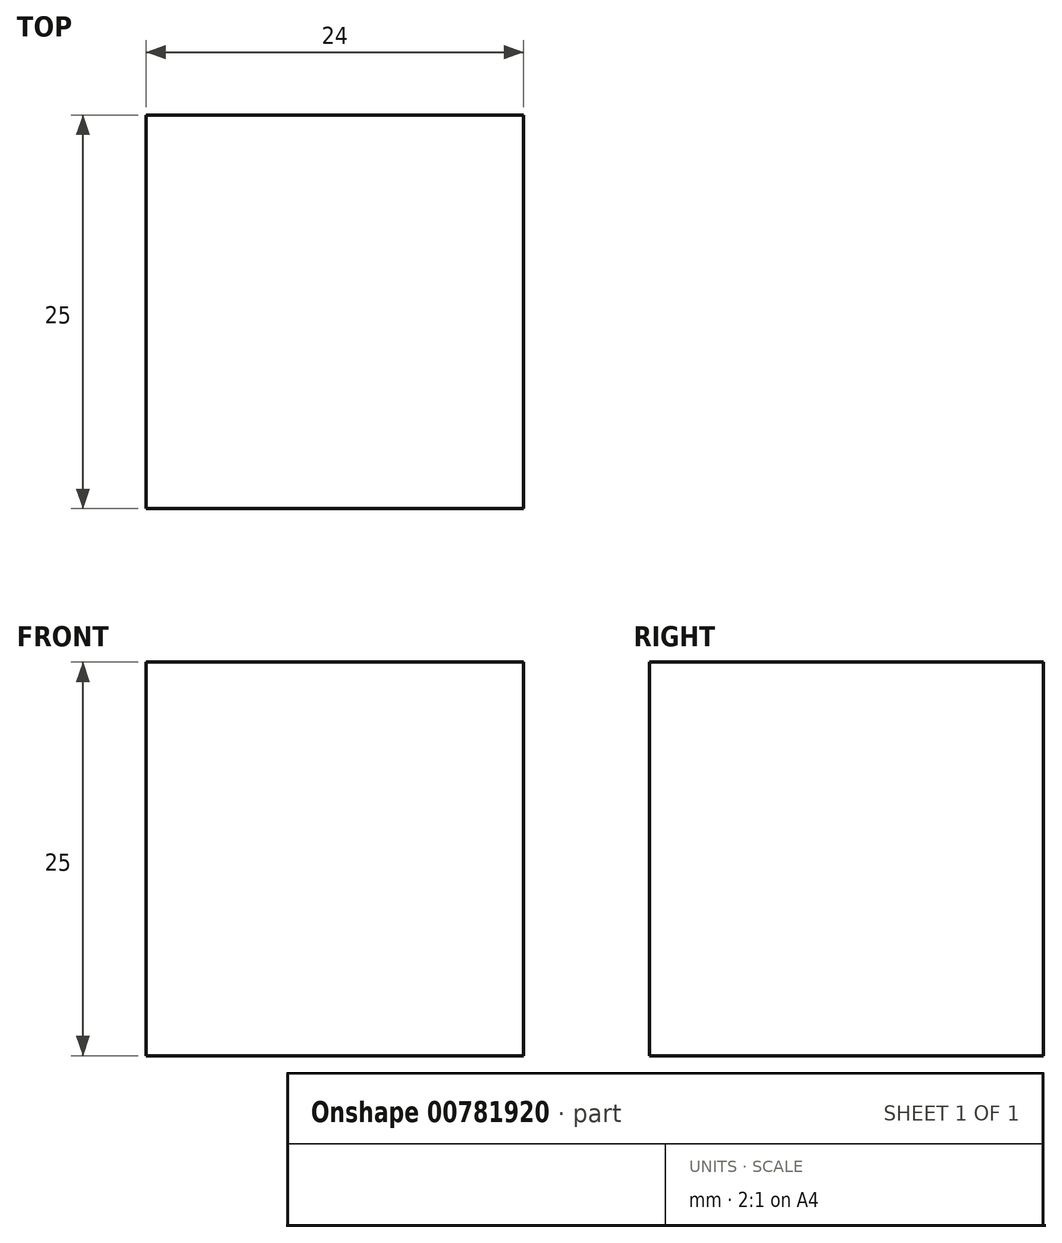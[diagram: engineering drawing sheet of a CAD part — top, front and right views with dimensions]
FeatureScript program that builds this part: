
annotation { "Feature Type Name" : "Feature", "Feature Type Description" : "" }
export const myFeature = defineFeature(function(context is Context, id is Id, definition is map)
    precondition{}
    {
        {
            var Q0;
            Q0=qCreatedBy(makeId("Front.planeOp"),FACE);
            var sketch = newSketch(context, id + "F0", { "sketchPlane" : qUnion([Q0])});
            skLineSegment(sketch, "E0.bottom", {"start": v(11.71, 12.54) * mm, "end": v(-13.29, 12.54) * mm});
            skLineSegment(sketch, "E0.top", {"start": v(11.71, -12.46) * mm, "end": v(-13.29, -12.46) * mm});
            skLineSegment(sketch, "E0.left", {"start": v(11.71, 12.54) * mm, "end": v(11.71, -12.46) * mm});
            skLineSegment(sketch, "E0.right", {"start": v(-12.29, 12.54) * mm, "end": v(-12.29, -12.46) * mm});
            skSolve(sketch);
        }
        {
            var Q0;
            Q0=qSketchRegion(id+"F0",true);
            extrude(context, id + "F1", {"entities" : qUnion([Q0]), "endBound" : BoundingType.SYMMETRIC, "depth" : 25 * mm, "offsetDistance" : 25 * mm});
        }
    });
